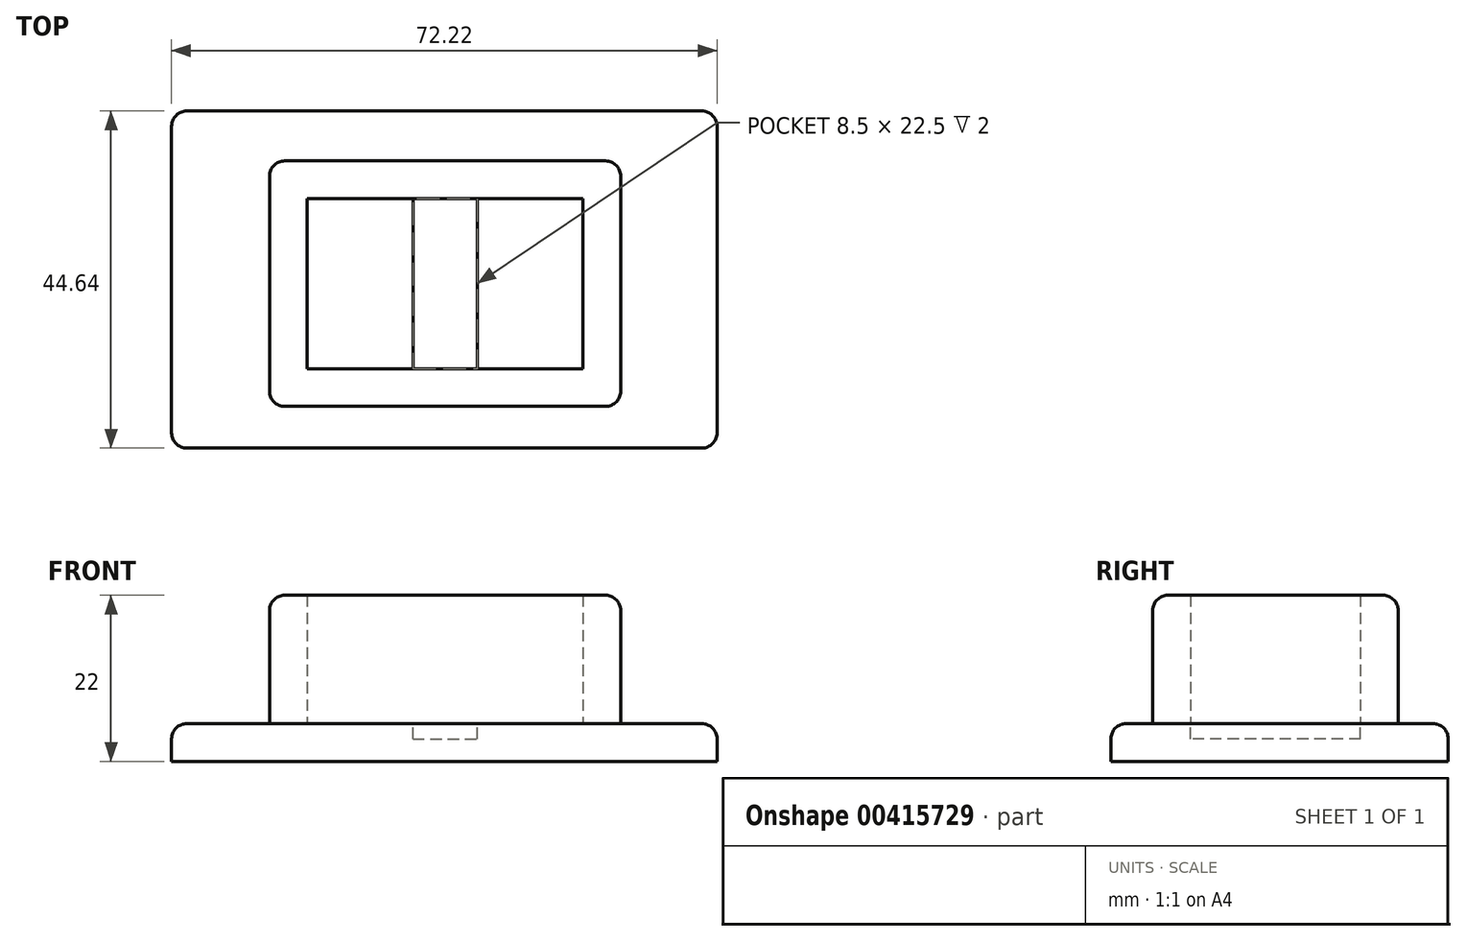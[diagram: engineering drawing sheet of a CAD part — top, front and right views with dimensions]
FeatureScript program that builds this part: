
annotation { "Feature Type Name" : "Feature", "Feature Type Description" : "" }
export const myFeature = defineFeature(function(context is Context, id is Id, definition is map)
    precondition{}
    {
        {
            var Q0;
            Q0=qCreatedBy(makeId("Top.planeOp"),FACE);
            var sketch = newSketch(context, id + "F0", { "sketchPlane" : qUnion([Q0])});
            skLineSegment(sketch, "E0.bottom", {"start": v(-18.15, 10.7) * mm, "end": v(18.35, 10.7) * mm});
            skLineSegment(sketch, "E0.top", {"start": v(-18.15, -11.8) * mm, "end": v(18.35, -11.8) * mm});
            skLineSegment(sketch, "E0.left", {"start": v(-18.15, 10.7) * mm, "end": v(-18.15, -11.8) * mm});
            skLineSegment(sketch, "E0.right", {"start": v(18.35, 10.7) * mm, "end": v(18.35, -11.8) * mm});
            skPoint(sketch, "E1", {"position": v(-18.15, -0.54) * mm});
            skPoint(sketch, "E2", {"position": v(0.1, 10.7) * mm});
            skLineSegment(sketch, "E3.bottom", {"start": v(-36.1, 22.32) * mm, "end": v(36.1, 22.32) * mm});
            skLineSegment(sketch, "E3.top", {"start": v(-36.1, -22.32) * mm, "end": v(36.1, -22.32) * mm});
            skLineSegment(sketch, "E3.left", {"start": v(-36.1, 22.32) * mm, "end": v(-36.1, -22.32) * mm});
            skLineSegment(sketch, "E3.right", {"start": v(36.1, 22.32) * mm, "end": v(36.1, -22.32) * mm});
            skPoint(sketch, "E3.middle", {"position": v(0, 0) * mm});
            skSolve(sketch);
        }
        {
            var Q0;
            Q0=makeQuery(id+"F0.imprint","IMPRINT",FACE,{"disambiguationData":[TD([[makeQuery(id+"F0.imprint","IMPRINT",EDGE,{"derivedFrom":sQuery(id+"F0.wireOp",EDGE,"E0.bottom")}),-1.0]])]});
            extrude(context, id + "F1", {"entities" : qUnion([Q0]), "depth" : 17 * mm});
        }
        {
            var Q0;
            Q0=makeQuery(id+"F1.opExtrude","CAP_FACE",FACE,{"disambiguationData":[OSD([sQuery(id+"F0.wireOp",EDGE,"E0.bottom"),sQuery(id+"F0.wireOp",EDGE,"E0.top"),sQuery(id+"F0.wireOp",EDGE,"E0.left"),sQuery(id+"F0.wireOp",EDGE,"E0.right")])],"isStart":false});
            shell(context, id + "F2", {"entities" : qUnion([Q0]), "thickness" : 5 * mm, "oppositeDirection" : true});
        }
        {
            var Q0;
            Q0=makeQuery(id+"F2.opShell","OFFSET_FACE",FACE,{"disambiguationData":[OSD([sQuery(id+"F0.wireOp",EDGE,"E0.bottom"),sQuery(id+"F0.wireOp",EDGE,"E0.top"),sQuery(id+"F0.wireOp",EDGE,"E0.left"),sQuery(id+"F0.wireOp",EDGE,"E0.right")])]});
            var sketch = newSketch(context, id + "F3", { "sketchPlane" : qUnion([Q0])});
            skLineSegment(sketch, "E4.bottom", {"start": v(-4.15, 10.7) * mm, "end": v(4.35, 10.7) * mm});
            skLineSegment(sketch, "E4.top", {"start": v(-4.15, -11.8) * mm, "end": v(4.35, -11.8) * mm});
            skLineSegment(sketch, "E4.left", {"start": v(-4.15, 10.7) * mm, "end": v(-4.15, -11.8) * mm});
            skLineSegment(sketch, "E4.right", {"start": v(4.35, 10.7) * mm, "end": v(4.35, -11.8) * mm});
            skSolve(sketch);
        }
        {
            var Q0;
            Q0=makeQuery(id+"F3.imprint","IMPRINT",FACE,{"disambiguationData":[TD([[makeQuery(id+"F3.imprint","IMPRINT",EDGE,{"derivedFrom":sQuery(id+"F3.wireOp",EDGE,"E4.bottom")}),-1.0]])]});
            extrude(context, id + "F4", {"entities" : qUnion([Q0]), "operationType" : NewBodyOperationType.REMOVE, "oppositeDirection" : true, "depth" : 2 * mm});
        }
        {
            var Q0;
            Q0 = qSketchRegion(id + "F0", true);
            extrude(context, id + "F5", {"entities" : qUnion([Q0]), "operationType" : NewBodyOperationType.ADD, "oppositeDirection" : true, "depth" : 5 * mm});
        }
        {
            var Q0;
            Q0=makeQuery(id+"F1.opExtrude","SWEPT_EDGE",EDGE,{"disambiguationData":[OSD([sQuery(id+"F0.wireOp",EDGE,"E0.top"),sQuery(id+"F0.wireOp",EDGE,"E0.left")])]});
            var Q1;
            Q1=makeQuery(id+"F1.opExtrude","SWEPT_EDGE",EDGE,{"disambiguationData":[OSD([sQuery(id+"F0.wireOp",EDGE,"E0.top"),sQuery(id+"F0.wireOp",EDGE,"E0.right")])]});
            var Q2;
            Q2=makeQuery(id+"F1.opExtrude","SWEPT_EDGE",EDGE,{"disambiguationData":[OSD([sQuery(id+"F0.wireOp",EDGE,"E0.bottom"),sQuery(id+"F0.wireOp",EDGE,"E0.right")])]});
            var Q3;
            Q3=makeQuery(id+"F1.opExtrude","SWEPT_EDGE",EDGE,{"disambiguationData":[OSD([sQuery(id+"F0.wireOp",EDGE,"E0.bottom"),sQuery(id+"F0.wireOp",EDGE,"E0.left")])]});
            var Q4;
            Q4=makeQuery(id+"F5.opExtrude","SWEPT_EDGE",EDGE,{"disambiguationData":[OSD([sQuery(id+"F0.wireOp",EDGE,"E3.top"),sQuery(id+"F0.wireOp",EDGE,"E3.right")])]});
            var Q5;
            Q5=makeQuery(id+"F5.opExtrude","SWEPT_EDGE",EDGE,{"disambiguationData":[OSD([sQuery(id+"F0.wireOp",EDGE,"E3.bottom"),sQuery(id+"F0.wireOp",EDGE,"E3.right")])]});
            var Q6;
            Q6=makeQuery(id+"F5.opExtrude","SWEPT_EDGE",EDGE,{"disambiguationData":[OSD([sQuery(id+"F0.wireOp",EDGE,"E3.top"),sQuery(id+"F0.wireOp",EDGE,"E3.left")])]});
            var Q7;
            Q7=makeQuery(id+"F5.opExtrude","SWEPT_EDGE",EDGE,{"disambiguationData":[OSD([sQuery(id+"F0.wireOp",EDGE,"E3.bottom"),sQuery(id+"F0.wireOp",EDGE,"E3.left")])]});
            fillet(context, id + "F6", {"entities" : qUnion([Q0, Q1, Q2, Q3, Q4, Q5, Q6, Q7]), "radius" : 2 * mm, "tangentPropagation" : true, "allowEdgeOverflow" : false});
        }
        {
            var Q0;
            Q0=makeQuery(id+"F1.opExtrude","CAP_EDGE",EDGE,{"disambiguationData":[OSD([sQuery(id+"F0.wireOp",EDGE,"E0.top")])],"isStart":false});
            var Q1;
            Q1=makeQuery(id+"F5.opExtrude","CAP_EDGE",EDGE,{"disambiguationData":[OSD([sQuery(id+"F0.wireOp",EDGE,"E3.top")])],"isStart":true});
            fillet(context, id + "F7", {"entities" : qUnion([Q0, Q1]), "radius" : 2 * mm, "tangentPropagation" : true, "allowEdgeOverflow" : false});
        }
    });
